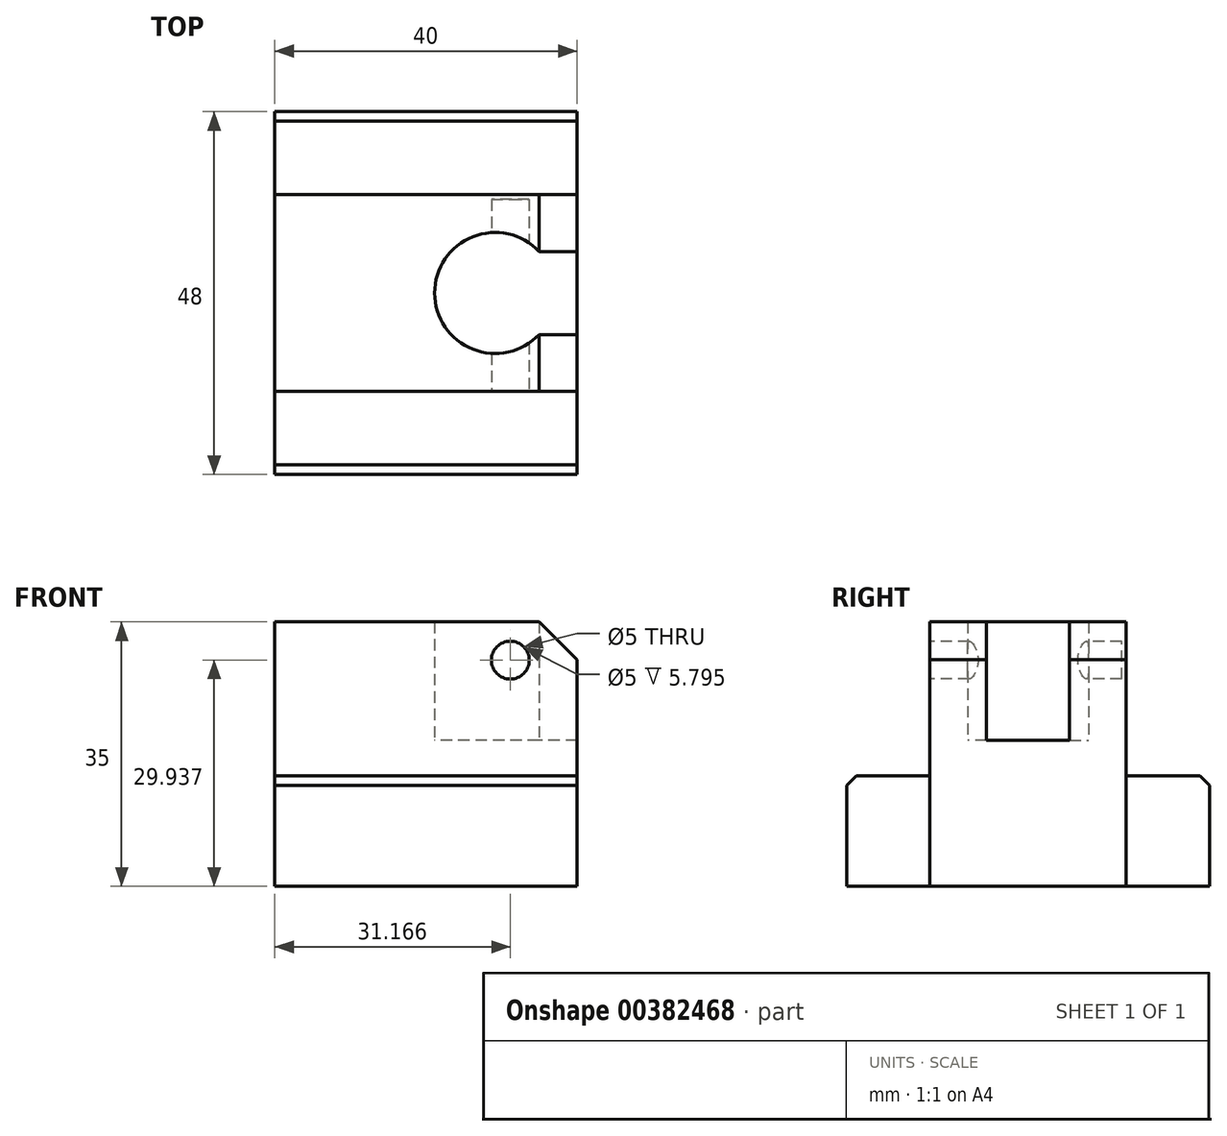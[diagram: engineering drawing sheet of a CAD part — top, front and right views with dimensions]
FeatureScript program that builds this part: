
annotation { "Feature Type Name" : "Feature", "Feature Type Description" : "" }
export const myFeature = defineFeature(function(context is Context, id is Id, definition is map)
    precondition{}
    {
        {
            var Q0;
            Q0=qCreatedBy(makeId("Top.planeOp"),FACE);
            var sketch = newSketch(context, id + "F0", { "sketchPlane" : qUnion([Q0])});
            skLineSegment(sketch, "E0.bottom", {"start": v(20, -24) * mm, "end": v(-20, -24) * mm});
            skLineSegment(sketch, "E0.top", {"start": v(20, 24) * mm, "end": v(-20, 24) * mm});
            skLineSegment(sketch, "E0.left", {"start": v(20, -24) * mm, "end": v(20, 24) * mm});
            skLineSegment(sketch, "E0.right", {"start": v(-20, -24) * mm, "end": v(-20, 24) * mm});
            skPoint(sketch, "E0.middle", {"position": v(0, 0) * mm});
            skLineSegment(sketch, "E1", {"start": v(-20, -13) * mm, "end": v(20, -13) * mm});
            skLineSegment(sketch, "E2", {"start": v(-20, 13) * mm, "end": v(20, 13) * mm});
            skLineSegment(sketch, "E3.bottom", {"start": v(20.01, 5.48) * mm, "end": v(14.98, 5.48) * mm});
            skLineSegment(sketch, "E3.top", {"start": v(20.01, -5.48) * mm, "end": v(14.98, -5.48) * mm});
            skLineSegment(sketch, "E3.left", {"start": v(20.01, 5.48) * mm, "end": v(20.01, -5.48) * mm});
            skPoint(sketch, "E3.middle", {"position": v(9.15, 0) * mm});
            skCircle(sketch, "E4", {"center": v(9.15, 0) * mm, "radius": 8 * mm});
            skPoint(sketch, "E3.right.end.orphan", {"position": v(-1.71, -5.48) * mm});
            skPoint(sketch, "E5.orphan", {"position": v(-1.71, 5.48) * mm});
            skSolve(sketch);
        }
        {
            var Q0;
            {var subQ0=sQuery(id+"F0.wireOp",EDGE,"E0.bottom");Q0=makeQuery(id+"F0.imprint","IMPRINT",FACE,{"disambiguationData":[TD([[makeQuery(id+"F0.imprint","IMPRINT",EDGE,{"derivedFrom":subQ0}),-1.0]])]});}
            var Q1;
            {var subQ0=sQuery(id+"F0.wireOp",EDGE,"E0.top");Q1=makeQuery(id+"F0.imprint","IMPRINT",FACE,{"disambiguationData":[TD([[makeQuery(id+"F0.imprint","IMPRINT",EDGE,{"derivedFrom":subQ0}),1.0]])]});}
            extrude(context, id + "F1", {"entities" : qUnion([Q0, Q1]), "depth" : 14.6 * mm});
        }
        {
            var Q0;
            {var subQ0=sQuery(id+"F0.wireOp",EDGE,"E1");Q0=makeQuery(id+"F0.imprint","IMPRINT",FACE,{"disambiguationData":[TD([[makeQuery(id+"F0.imprint","IMPRINT",EDGE,{"derivedFrom":subQ0}),1.0]])]});}
            extrude(context, id + "F2", {"entities" : qUnion([Q0]), "depth" : 35 * mm});
        }
        {
            var Q0;
            {var subQ0=sQuery(id+"F0.wireOp",EDGE,"E4");var subQ1=makeQuery(id+"F0.imprint","INTERSECT",VERTEX,{"derivedFrom":[sQuery(id+"F0.wireOp",EDGE,"E3.bottom"),subQ0]});Q0=makeQuery(id+"F0.imprint","IMPRINT",FACE,{"disambiguationData":[TD([[makeQuery(id+"F0.imprint","IMPRINT",EDGE,{"disambiguationData":[TD([[subQ1,-1.0]])],"derivedFrom":subQ0}),1.0]])]});}
            var Q1;
            {var subQ0=sQuery(id+"F0.wireOp",EDGE,"E3.top");var subQ1=sQuery(id+"F0.wireOp",EDGE,"E0.left");var subQ2=makeQuery(id+"F0.imprint","INTERSECT",VERTEX,{"derivedFrom":[subQ1,subQ0]});Q1=makeQuery(id+"F0.imprint","IMPRINT",FACE,{"disambiguationData":[TD([[makeQuery(id+"F0.imprint","IMPRINT",EDGE,{"disambiguationData":[TD([[subQ2,-1.0]])],"derivedFrom":subQ1}),1.0]])]});}
            extrude(context, id + "F3", {"entities" : qUnion([Q0, Q1]), "operationType" : NewBodyOperationType.ADD, "depth" : 19.3 * mm});
        }
        {
            var Q0;
            {var subQ0=sQuery(id+"F0.wireOp",EDGE,"E0.left");Q0=makeQuery(id+"F2.opExtrude","CAP_EDGE",EDGE,{"disambiguationData":[OSD([subQ0]),TDD([makeQuery(id+"F0.imprint","IMPRINT",EDGE,{"disambiguationData":[TD([[makeQuery(id+"F0.imprint","INTERSECT",VERTEX,{"derivedFrom":[subQ0,sQuery(id+"F0.wireOp",EDGE,"E1")]}),-1.0]])],"derivedFrom":subQ0})])],"isStart":false});}
            var Q1;
            {var subQ0=sQuery(id+"F0.wireOp",EDGE,"E0.left");Q1=makeQuery(id+"F2.opExtrude","CAP_EDGE",EDGE,{"disambiguationData":[OSD([subQ0]),TDD([makeQuery(id+"F0.imprint","IMPRINT",EDGE,{"disambiguationData":[TD([[makeQuery(id+"F0.imprint","INTERSECT",VERTEX,{"derivedFrom":[subQ0,sQuery(id+"F0.wireOp",EDGE,"E2")]}),1.0]])],"derivedFrom":subQ0})])],"isStart":false});}
            chamfer(context, id + "F4", {"entities" : qUnion([Q0, Q1]), "width" : 5 * mm, "tangentPropagation" : true});
        }
        {
            var Q0;
            Q0=makeQuery(id+"F2.opExtrude","SWEPT_FACE",FACE,{"disambiguationData":[OSD([sQuery(id+"F0.wireOp",EDGE,"E1")])]});
            var sketch = newSketch(context, id + "F5", { "sketchPlane" : qUnion([Q0])});
            skCircle(sketch, "E6", {"center": v(11.17, 29.94) * mm, "radius": 2.5 * mm});
            skSolve(sketch);
        }
        {
            var Q0;
            Q0 = qSketchRegion(id + "F5", true);
            extrude(context, id + "F6", {"entities" : qUnion([Q0]), "operationType" : NewBodyOperationType.REMOVE, "oppositeDirection" : true, "depth" : 25.4 * mm});
        }
        {
            var Q0;
            Q0=makeQuery(id+"F1.opExtrude","CAP_EDGE",EDGE,{"disambiguationData":[OSD([sQuery(id+"F0.wireOp",EDGE,"E0.top")])],"isStart":false});
            var Q1;
            Q1=makeQuery(id+"F1.opExtrude","CAP_EDGE",EDGE,{"disambiguationData":[OSD([sQuery(id+"F0.wireOp",EDGE,"E0.bottom")])],"isStart":false});
            chamfer(context, id + "F7", {"entities" : qUnion([Q0, Q1]), "width" : 1.27 * mm, "tangentPropagation" : true});
        }
    });
